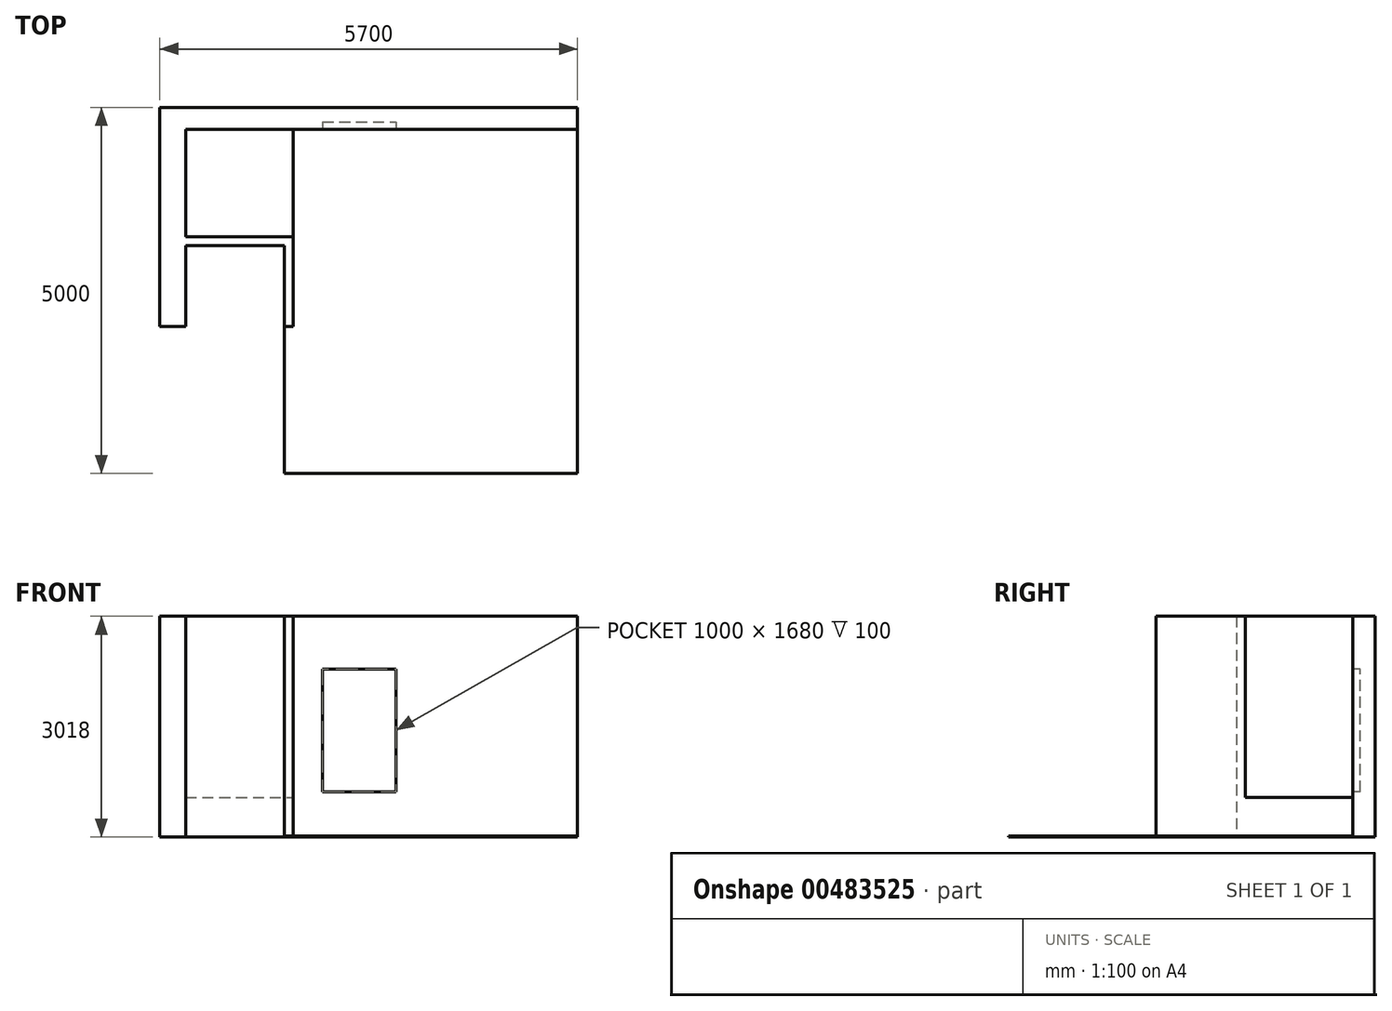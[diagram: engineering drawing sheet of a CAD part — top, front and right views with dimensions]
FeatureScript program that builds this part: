
annotation { "Feature Type Name" : "Feature", "Feature Type Description" : "" }
export const myFeature = defineFeature(function(context is Context, id is Id, definition is map)
    precondition{}
    {
        {
            var Q0;
            Q0=qCreatedBy(makeId("Top.planeOp"),FACE);
            var sketch = newSketch(context, id + "F0", { "sketchPlane" : qUnion([Q0])});
            skLineSegment(sketch, "E0.bottom", {"start": v(0, 0) * mm, "end": v(4000, 0) * mm});
            skLineSegment(sketch, "E0.top", {"start": v(0, -5000) * mm, "end": v(4000, -5000) * mm});
            skLineSegment(sketch, "E0.left", {"start": v(0, 0) * mm, "end": v(0, -5000) * mm});
            skLineSegment(sketch, "E0.right", {"start": v(4000, 0) * mm, "end": v(4000, -5000) * mm});
            skSolve(sketch);
        }
        {
            var Q0;
            Q0=makeQuery(id+"F0.imprint","IMPRINT",FACE,{"disambiguationData":[TD([[makeQuery(id+"F0.imprint","IMPRINT",EDGE,{"derivedFrom":sQuery(id+"F0.wireOp",EDGE,"E0.bottom")}),-1.0]])]});
            extrude(context, id + "F1", {"entities" : qUnion([Q0]), "depth" : 18 * mm});
        }
        {
            var Q0;
            Q0=makeQuery(id+"F1.opExtrude","CAP_FACE",FACE,{"disambiguationData":[OSD([sQuery(id+"F0.wireOp",EDGE,"E0.bottom"),sQuery(id+"F0.wireOp",EDGE,"E0.top"),sQuery(id+"F0.wireOp",EDGE,"E0.left"),sQuery(id+"F0.wireOp",EDGE,"E0.right")])],"isStart":false});
            var sketch = newSketch(context, id + "F2", { "sketchPlane" : qUnion([Q0])});
            skLineSegment(sketch, "E1.bottom", {"start": v(0, 0) * mm, "end": v(4000, 0) * mm});
            skLineSegment(sketch, "E1.top", {"start": v(0, -300) * mm, "end": v(4000, -300) * mm});
            skLineSegment(sketch, "E1.left", {"start": v(0, 0) * mm, "end": v(0, -300) * mm});
            skLineSegment(sketch, "E1.right", {"start": v(4000, 0) * mm, "end": v(4000, -300) * mm});
            skSolve(sketch);
        }
        {
            var Q0;
            Q0 = qSketchRegion(id + "F2", true);
            extrude(context, id + "F3", {"entities" : qUnion([Q0]), "operationType" : NewBodyOperationType.ADD, "depth" : 3000 * mm});
        }
        {
            var Q0;
            Q0=makeQuery(id+"F1.opExtrude","CAP_FACE",FACE,{"disambiguationData":[OSD([sQuery(id+"F0.wireOp",EDGE,"E0.bottom"),sQuery(id+"F0.wireOp",EDGE,"E0.top"),sQuery(id+"F0.wireOp",EDGE,"E0.left"),sQuery(id+"F0.wireOp",EDGE,"E0.right")])],"isStart":false});
            var sketch = newSketch(context, id + "F4", { "sketchPlane" : qUnion([Q0])});
            skLineSegment(sketch, "E2.bottom", {"start": v(0, -300) * mm, "end": v(120, -300) * mm});
            skLineSegment(sketch, "E2.top", {"start": v(0, -2990) * mm, "end": v(120, -2990) * mm});
            skLineSegment(sketch, "E2.left", {"start": v(0, -300) * mm, "end": v(0, -2990) * mm});
            skLineSegment(sketch, "E2.right", {"start": v(120, -300) * mm, "end": v(120, -2990) * mm});
            skSolve(sketch);
        }
        {
            var Q0;
            Q0 = qSketchRegion(id + "F4", true);
            extrude(context, id + "F5", {"entities" : qUnion([Q0]), "operationType" : NewBodyOperationType.ADD, "depth" : 525 * mm});
        }
        {
            var Q0;
            Q0=makeQuery(id+"F5.opExtrude","SWEPT_FACE",FACE,{"disambiguationData":[OSD([sQuery(id+"F4.wireOp",EDGE,"E2.right")])]});
            var sketch = newSketch(context, id + "F6", { "sketchPlane" : qUnion([Q0])});
            skLineSegment(sketch, "E3.bottom", {"start": v(-2990, 543) * mm, "end": v(-1770, 543) * mm});
            skLineSegment(sketch, "E3.top", {"start": v(-2990, 3018) * mm, "end": v(-1770, 3018) * mm});
            skLineSegment(sketch, "E3.left", {"start": v(-2990, 543) * mm, "end": v(-2990, 3018) * mm});
            skLineSegment(sketch, "E3.right", {"start": v(-1770, 543) * mm, "end": v(-1770, 3018) * mm});
            skPoint(sketch, "E4.0", {"position": v(-300, 3018) * mm});
            skSolve(sketch);
        }
        {
            var Q0;
            Q0 = qSketchRegion(id + "F6", true);
            var Q1;
            Q1=makeQuery(id+"F5.boolean.opBoolean","MERGE",FACE,{"derivedFrom":[makeQuery(id+"F3.boolean.opBoolean","MERGE",FACE,{"derivedFrom":[makeQuery(id+"F1.opExtrude","SWEPT_FACE",FACE,{"disambiguationData":[OSD([sQuery(id+"F0.wireOp",EDGE,"E0.left")])]}),makeQuery(id+"F3.opExtrude","SWEPT_FACE",FACE,{"disambiguationData":[OSD([sQuery(id+"F2.wireOp",EDGE,"E1.left")])]})]}),makeQuery(id+"F5.opExtrude","SWEPT_FACE",FACE,{"disambiguationData":[OSD([sQuery(id+"F4.wireOp",EDGE,"E2.left")])]})]});
            extrude(context, id + "F7", {"entities" : qUnion([Q0]), "operationType" : NewBodyOperationType.ADD, "endBound" : BoundingType.UP_TO_SURFACE, "oppositeDirection" : true, "endBoundEntityFace" : qUnion([Q1]), "depth" : 25 * mm});
        }
        {
            var Q0;
            Q0=makeQuery(id+"F7.boolean.opBoolean","MERGE",FACE,{"derivedFrom":[makeQuery(id+"F5.boolean.opBoolean","MERGE",FACE,{"derivedFrom":[makeQuery(id+"F3.boolean.opBoolean","MERGE",FACE,{"derivedFrom":[makeQuery(id+"F1.opExtrude","SWEPT_FACE",FACE,{"disambiguationData":[OSD([sQuery(id+"F0.wireOp",EDGE,"E0.left")])]}),makeQuery(id+"F3.opExtrude","SWEPT_FACE",FACE,{"disambiguationData":[OSD([sQuery(id+"F2.wireOp",EDGE,"E1.left")])]})]}),makeQuery(id+"F5.opExtrude","SWEPT_FACE",FACE,{"disambiguationData":[OSD([sQuery(id+"F4.wireOp",EDGE,"E2.left")])]})]}),makeQuery(id+"F7.opExtrude","CAP_FACE",FACE,{"disambiguationData":[OSD([sQuery(id+"F6.wireOp",EDGE,"E3.bottom"),sQuery(id+"F6.wireOp",EDGE,"E3.top"),sQuery(id+"F6.wireOp",EDGE,"E3.left"),sQuery(id+"F6.wireOp",EDGE,"E3.right")])],"isStart":false})]});
            var sketch = newSketch(context, id + "F8", { "sketchPlane" : qUnion([Q0])});
            skLineSegment(sketch, "E5.0", {"start": v(0, 3018) * mm, "end": v(0, 0) * mm});
            skPoint(sketch, "E6.0", {"position": v(150, 3018) * mm});
            skLineSegment(sketch, "E7.0", {"start": v(300, 3018) * mm, "end": v(300, 543) * mm});
            skLineSegment(sketch, "E8.0", {"start": v(300, 543) * mm, "end": v(1770, 543) * mm});
            skLineSegment(sketch, "E9.0", {"start": v(1770, 3018) * mm, "end": v(1770, 543) * mm});
            skLineSegment(sketch, "E10.0", {"start": v(1770, 3018) * mm, "end": v(1890, 3018) * mm});
            skLineSegment(sketch, "E11.0", {"start": v(0, 0) * mm, "end": v(5000, 0) * mm});
            skLineSegment(sketch, "E12", {"start": v(1890, 3018) * mm, "end": v(1890, 0) * mm});
            skPoint(sketch, "E13.orphan", {"position": v(2990, 3018) * mm});
            skSolve(sketch);
        }
        {
            var Q0;
            Q0 = qSketchRegion(id + "F8", true);
            var Q1;
            {var subQ0=sQuery(id+"F8.wireOp",EDGE,"E5.0");Q1=makeQuery(id+"F8.imprint","IMPRINT",FACE,{"disambiguationData":[TD([[makeQuery(id+"F8.imprint","IMPRINT",EDGE,{"derivedFrom":subQ0}),1.0]])]});}
            extrude(context, id + "F9", {"entities" : qUnion([Q0, Q1]), "operationType" : NewBodyOperationType.ADD, "depth" : 1350 * mm});
        }
        {
            var Q0;
            Q0=makeQuery(id+"F9.opExtrude","CAP_FACE",FACE,{"disambiguationData":[OSD([sQuery(id+"F2.wireOp",EDGE,"E1.left"),sQuery(id+"F8.wireOp",EDGE,"E5.0"),sQuery(id+"F8.wireOp",EDGE,"E7.0"),sQuery(id+"F8.wireOp",EDGE,"E8.0"),sQuery(id+"F8.wireOp",EDGE,"E9.0"),sQuery(id+"F8.wireOp",EDGE,"E10.0"),sQuery(id+"F8.wireOp",EDGE,"E11.0"),sQuery(id+"F8.wireOp",EDGE,"E12")])],"isStart":false});
            var sketch = newSketch(context, id + "F10", { "sketchPlane" : qUnion([Q0])});
            skLineSegment(sketch, "E14.bottom", {"start": v(0, 0) * mm, "end": v(2990, 0) * mm});
            skLineSegment(sketch, "E14.top", {"start": v(0, 3018) * mm, "end": v(2990, 3018) * mm});
            skLineSegment(sketch, "E14.left", {"start": v(0, 0) * mm, "end": v(0, 3018) * mm});
            skLineSegment(sketch, "E14.right", {"start": v(2990, 0) * mm, "end": v(2990, 3018) * mm});
            skPoint(sketch, "E15.0", {"position": v(2990, 3018) * mm});
            skSolve(sketch);
        }
        {
            var Q0;
            Q0 = qSketchRegion(id + "F10", true);
            extrude(context, id + "F11", {"entities" : qUnion([Q0]), "operationType" : NewBodyOperationType.ADD, "depth" : 350 * mm});
        }
        {
            var Q0;
            Q0=makeQuery(id+"F9.boolean.opBoolean","MERGE",FACE,{"derivedFrom":[makeQuery(id+"F3.opExtrude","SWEPT_FACE",FACE,{"disambiguationData":[OSD([sQuery(id+"F2.wireOp",EDGE,"E1.top")])]}),makeQuery(id+"F9.opExtrude","SWEPT_FACE",FACE,{"disambiguationData":[OSD([sQuery(id+"F8.wireOp",EDGE,"E7.0")])]})]});
            var sketch = newSketch(context, id + "F12", { "sketchPlane" : qUnion([Q0])});
            skLineSegment(sketch, "E16.bottom", {"start": v(520, 618) * mm, "end": v(1520, 618) * mm});
            skLineSegment(sketch, "E16.top", {"start": v(520, 2298) * mm, "end": v(1520, 2298) * mm});
            skLineSegment(sketch, "E16.left", {"start": v(520, 618) * mm, "end": v(520, 2298) * mm});
            skLineSegment(sketch, "E16.right", {"start": v(1520, 618) * mm, "end": v(1520, 2298) * mm});
            skSolve(sketch);
        }
        {
            var Q0;
            Q0 = qSketchRegion(id + "F12", true);
            extrude(context, id + "F13", {"entities" : qUnion([Q0]), "operationType" : NewBodyOperationType.REMOVE, "oppositeDirection" : true, "depth" : 100 * mm});
        }
    });
